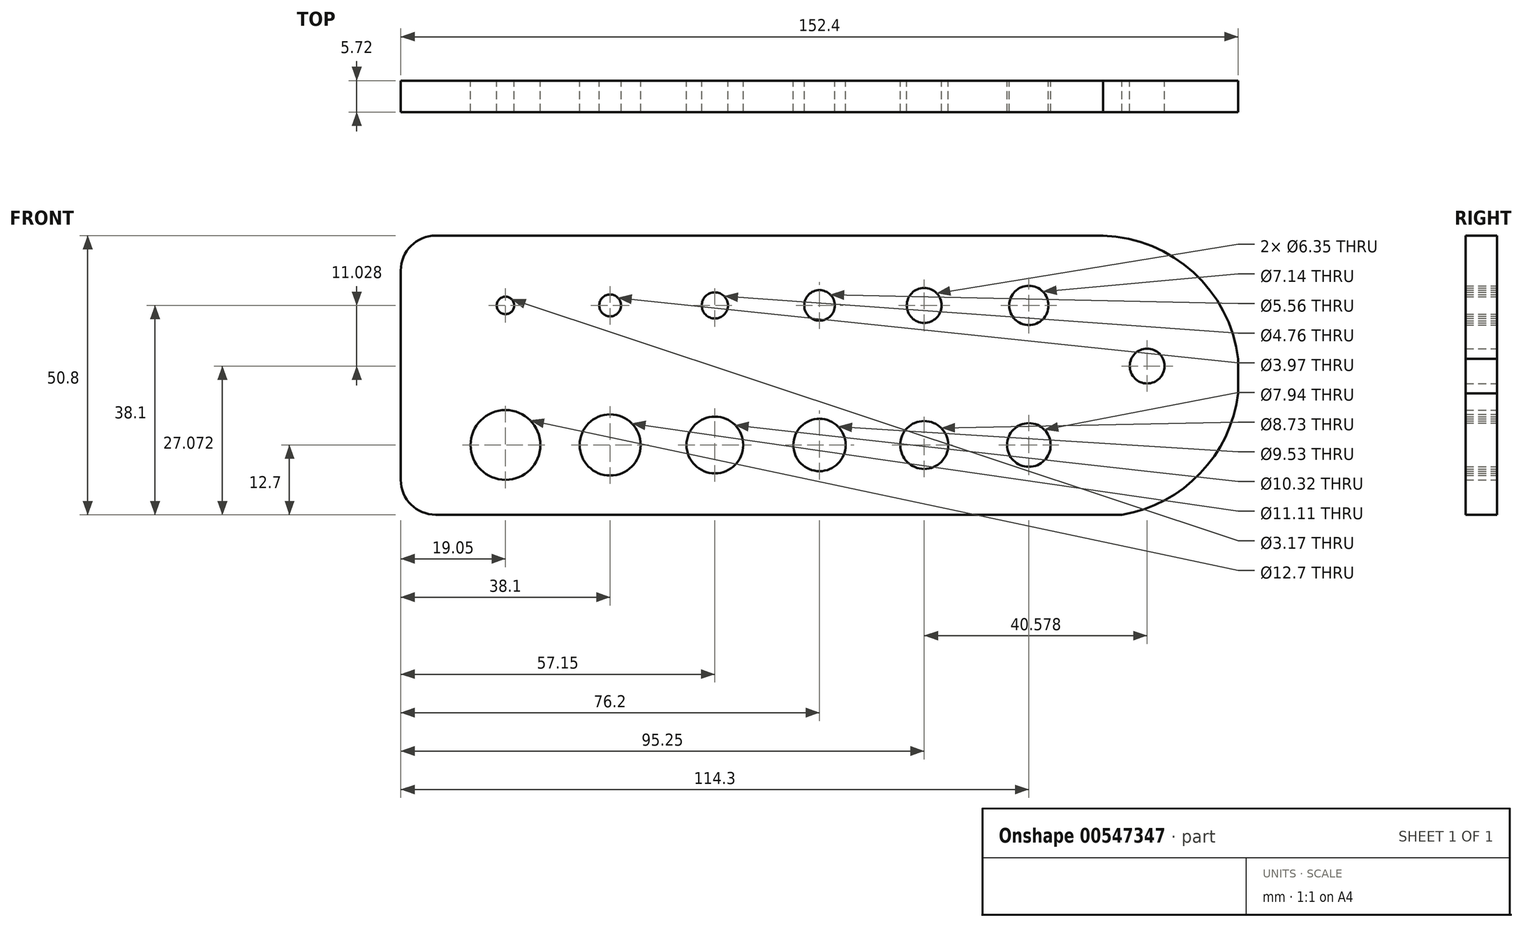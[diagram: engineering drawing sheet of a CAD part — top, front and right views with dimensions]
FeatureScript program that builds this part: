
annotation { "Feature Type Name" : "Feature", "Feature Type Description" : "" }
export const myFeature = defineFeature(function(context is Context, id is Id, definition is map)
    precondition{}
    {
        {
            var Q0;
            Q0=qCreatedBy(makeId("Front.planeOp"),FACE);
            var sketch = newSketch(context, id + "F0", { "sketchPlane" : qUnion([Q0])});
            skLineSegment(sketch, "E0.bottom", {"start": v(6.35, 0) * mm, "end": v(131.2, 0) * mm});
            skLineSegment(sketch, "E0.top", {"start": v(6.35, 50.8) * mm, "end": v(127.8, 50.8) * mm});
            skLineSegment(sketch, "E0.left", {"start": v(0, 6.35) * mm, "end": v(0, 44.45) * mm});
            skLineSegment(sketch, "E0.right", {"start": v(152.4, 22.11) * mm, "end": v(152.4, 28.35) * mm});
            skPoint(sketch, "E1.visualSharp", {"position": v(0, 50.8) * mm});
            skArc(sketch, "E1.filletArc", {"start": v(6.35, 50.8) * mm, "mid": v(1.86, 48.94) * mm, "end": v(0, 44.45) * mm});
            skPoint(sketch, "E2.visualSharp", {"position": v(0, 0) * mm});
            skArc(sketch, "E2.filletArc", {"start": v(0, 6.35) * mm, "mid": v(1.86, 1.86) * mm, "end": v(6.35, 0) * mm});
            skPoint(sketch, "E3.endSnap0", {"position": v(152.4, 25.4) * mm});
            skArc(sketch, "E4", {"start": v(131.2, 0) * mm, "mid": v(152.53, 26.94) * mm, "end": v(127.8, 50.8) * mm});
            skPoint(sketch, "E5.orphan", {"position": v(152.4, 50.8) * mm});
            skPoint(sketch, "E6.orphan", {"position": v(152.4, 0) * mm});
            skCircle(sketch, "E7", {"center": v(19.05, 12.7) * mm, "radius": 6.35 * mm});
            skCircle(sketch, "E8", {"center": v(19.05, 38.1) * mm, "radius": 1.59 * mm});
            skCircle(sketch, "E9.1.0.0", {"center": v(38.1, 12.7) * mm, "radius": 5.56 * mm});
            skCircle(sketch, "E9.2.0.0", {"center": v(57.15, 12.7) * mm, "radius": 5.16 * mm});
            skCircle(sketch, "E9.3.0.0", {"center": v(76.2, 12.7) * mm, "radius": 4.76 * mm});
            skCircle(sketch, "E9.4.0.0", {"center": v(95.25, 12.7) * mm, "radius": 4.37 * mm});
            skCircle(sketch, "E9.5.0.0", {"center": v(114.3, 12.7) * mm, "radius": 3.97 * mm});
            skLineSegment(sketch, "E9.direction1", {"start": v(19.05, 12.7) * mm, "end": v(38.1, 12.7) * mm, "construction": true});
            skCircle(sketch, "E10.1.0.0", {"center": v(38.1, 38.1) * mm, "radius": 1.98 * mm});
            skCircle(sketch, "E10.2.0.0", {"center": v(57.15, 38.1) * mm, "radius": 2.38 * mm});
            skCircle(sketch, "E10.3.0.0", {"center": v(76.2, 38.1) * mm, "radius": 2.78 * mm});
            skCircle(sketch, "E10.4.0.0", {"center": v(95.25, 38.1) * mm, "radius": 3.18 * mm});
            skCircle(sketch, "E10.5.0.0", {"center": v(114.3, 38.1) * mm, "radius": 3.57 * mm});
            skLineSegment(sketch, "E10.direction1", {"start": v(19.05, 38.1) * mm, "end": v(38.1, 38.1) * mm, "construction": true});
            skCircle(sketch, "E11", {"center": v(135.83, 27.07) * mm, "radius": 3.18 * mm});
            skSolve(sketch);
        }
        {
            var Q0;
            {var subQ3=sQuery(id+"F0.wireOp",EDGE,"E0.bottom");Q0=makeQuery(id+"F0.imprint","IMPRINT",FACE,{"disambiguationData":[TD([[makeQuery(id+"F0.imprint","IMPRINT",EDGE,{"derivedFrom":subQ3}),1.0]])]});}
            extrude(context, id + "F1", {"entities" : qUnion([Q0]), "depth" : 5.7 * mm, "offsetDistance" : 25.4 * mm});
        }
    });
